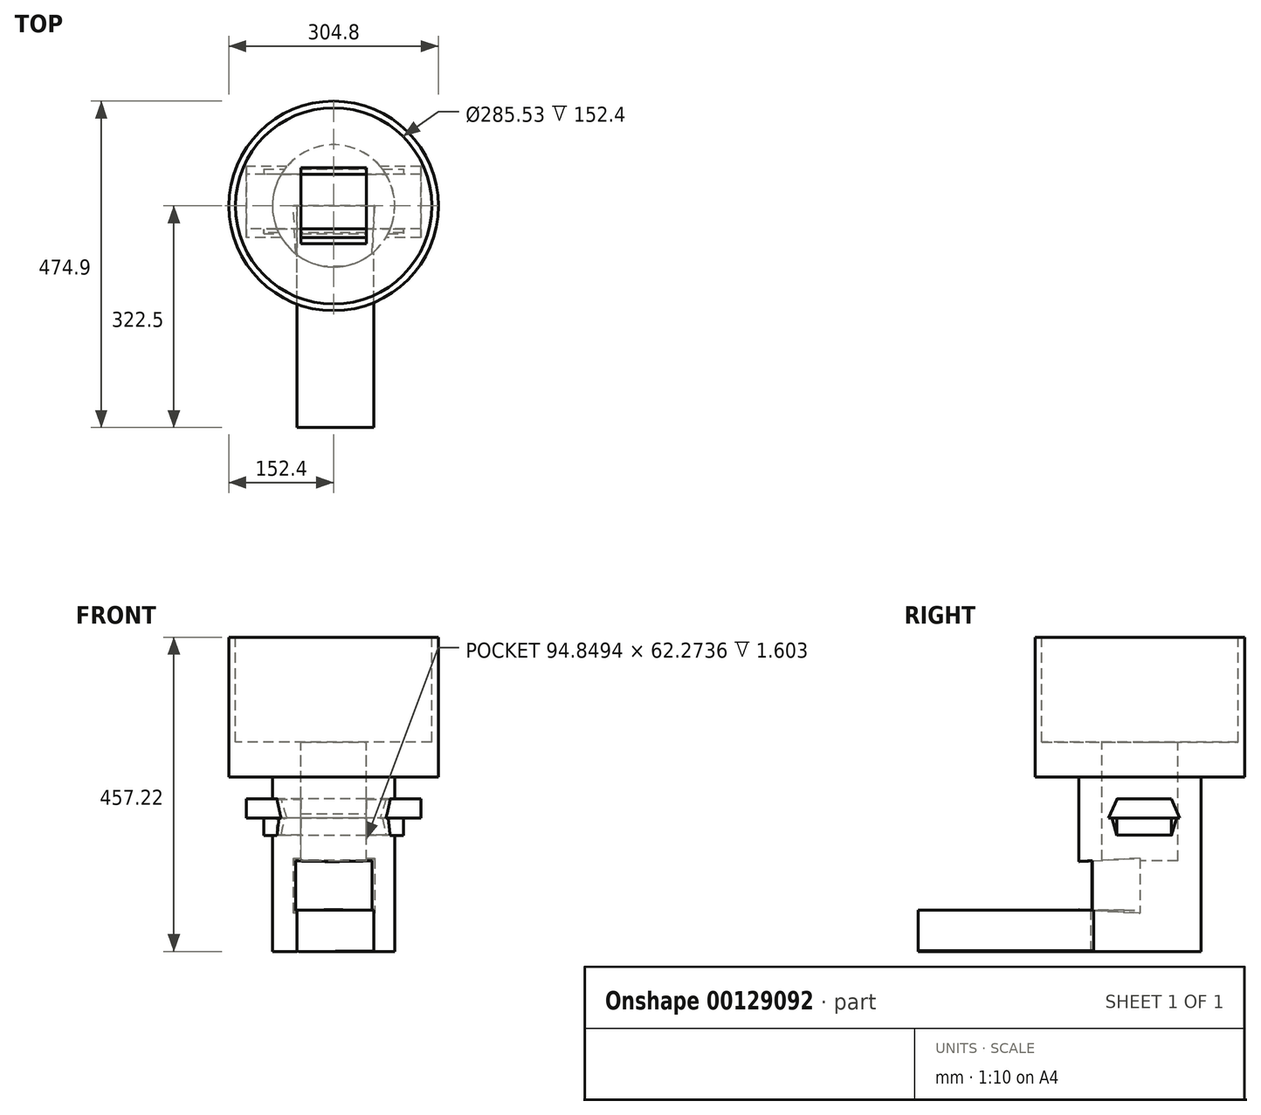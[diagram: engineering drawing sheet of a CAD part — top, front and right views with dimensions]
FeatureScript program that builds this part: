
annotation { "Feature Type Name" : "Feature", "Feature Type Description" : "" }
export const myFeature = defineFeature(function(context is Context, id is Id, definition is map)
    precondition{}
    {
        {
            var Q0;
            Q0=qCreatedBy(makeId("Top.planeOp"),FACE);
            var sketch = newSketch(context, id + "F0", { "sketchPlane" : qUnion([Q0])});
            skCircle(sketch, "E0", {"center": v(0, 0) * mm, "radius": 152.4 * mm});
            skSolve(sketch);
        }
        {
            var Q0;
            Q0 = qSketchRegion(id + "F0", true);
            extrude(context, id + "F1", {"entities" : qUnion([Q0]), "depth" : 203.2 * mm});
        }
        {
            var Q0;
            Q0=makeQuery(id+"F1.opExtrude","CAP_FACE",FACE,{"disambiguationData":[OSD([sQuery(id+"F0.wireOp",EDGE,"E0")])],"isStart":true});
            var sketch = newSketch(context, id + "F2", { "sketchPlane" : qUnion([Q0])});
            skCircle(sketch, "E1", {"center": v(0, 0) * mm, "radius": 88.9 * mm});
            skSolve(sketch);
        }
        {
            var Q0;
            Q0=makeQuery(id+"F2.imprint","IMPRINT",FACE,{"disambiguationData":[TD([[makeQuery(id+"F2.imprint","IMPRINT",EDGE,{"derivedFrom":sQuery(id+"F2.wireOp",EDGE,"E1")}),1.0]])]});
            extrude(context, id + "F3", {"entities" : qUnion([Q0]), "operationType" : NewBodyOperationType.ADD, "depth" : 254 * mm});
        }
        {
            var Q0;
            Q0=qCreatedBy(makeId("Front.planeOp"),FACE);
            var sketch = newSketch(context, id + "F4", { "sketchPlane" : qUnion([Q0])});
            skLineSegment(sketch, "E2.bottom", {"start": v(-58.57, -118.54) * mm, "end": v(59.53, -118.54) * mm});
            skLineSegment(sketch, "E2.top", {"start": v(-58.57, -198.23) * mm, "end": v(59.53, -198.23) * mm});
            skLineSegment(sketch, "E2.left", {"start": v(-58.57, -118.54) * mm, "end": v(-58.57, -198.23) * mm});
            skLineSegment(sketch, "E2.right", {"start": v(59.53, -118.54) * mm, "end": v(59.53, -198.23) * mm});
            skSolve(sketch);
        }
        {
            var Q0;
            Q0 = qSketchRegion(id + "F4", true);
            var Q1;
            Q1=makeQuery(id+"F1.opExtrude","SWEPT_BODY",BODY,{"disambiguationData":[OSD([sQuery(id+"F0.wireOp",EDGE,"E0")])]});
            extrude(context, id + "F5", {"entities" : qUnion([Q0]), "operationType" : NewBodyOperationType.REMOVE, "endBoundEntityBody" : qUnion([Q1]), "depth" : 152.4 * mm, "hasDraft" : true, "draftAngle" : 3 * degree, "draftPullDirection" : true});
        }
        {
            var Q0;
            Q0=makeQuery(id+"F1.opExtrude","CAP_FACE",FACE,{"disambiguationData":[OSD([sQuery(id+"F0.wireOp",EDGE,"E0")])],"isStart":false});
            var sketch = newSketch(context, id + "F6", { "sketchPlane" : qUnion([Q0])});
            skLineSegment(sketch, "E3.bottom", {"start": v(47.42, 55.23) * mm, "end": v(-47.42, 55.23) * mm});
            skLineSegment(sketch, "E3.top", {"start": v(47.42, -55.23) * mm, "end": v(-47.42, -55.23) * mm});
            skLineSegment(sketch, "E3.left", {"start": v(47.42, 55.23) * mm, "end": v(47.42, -55.23) * mm});
            skLineSegment(sketch, "E3.right", {"start": v(-47.42, 55.23) * mm, "end": v(-47.42, -55.23) * mm});
            skPoint(sketch, "E3.middle", {"position": v(0, 0) * mm});
            skSolve(sketch);
        }
        {
            var Q0;
            Q0=makeQuery(id+"F6.imprint","IMPRINT",FACE,{"disambiguationData":[TD([[makeQuery(id+"F6.imprint","IMPRINT",EDGE,{"derivedFrom":sQuery(id+"F6.wireOp",EDGE,"E3.bottom")}),1.0]])]});
            var Q1;
            Q1=sQuery(id+"F6.wireOp",EDGE,"bKwGgYF3-I8BH-BRHj-HJDU-NQ5mYMks3KpP");
            extrude(context, id + "F7", {"entities" : qUnion([Q0]), "operationType" : NewBodyOperationType.REMOVE, "surfaceEntities" : qUnion([Q1]), "oppositeDirection" : true, "depth" : 325.12 * mm});
        }
        {
            var Q0;
            Q0=makeQuery(id+"F1.opExtrude","CAP_FACE",FACE,{"disambiguationData":[OSD([sQuery(id+"F0.wireOp",EDGE,"E0")])],"isStart":false});
            var sketch = newSketch(context, id + "F8", { "sketchPlane" : qUnion([Q0])});
            skCircle(sketch, "E4", {"center": v(0, 0) * mm, "radius": 142.76 * mm});
            skSolve(sketch);
        }
        {
            var Q0;
            Q0 = qSketchRegion(id + "F8", true);
            extrude(context, id + "F9", {"entities" : qUnion([Q0]), "operationType" : NewBodyOperationType.REMOVE, "oppositeDirection" : true, "depth" : 152.4 * mm});
        }
        {
            var Q0;
            Q0=qCreatedBy(makeId("Right.planeOp"),FACE);
            var sketch = newSketch(context, id + "F10", { "sketchPlane" : qUnion([Q0])});
            skLineSegment(sketch, "E5.bottom", {"start": v(-33.68, -32.13) * mm, "end": v(46.01, -32.13) * mm});
            skLineSegment(sketch, "E5.top", {"start": v(-33.68, -84.93) * mm, "end": v(46.01, -84.93) * mm});
            skLineSegment(sketch, "E5.left", {"start": v(-33.68, -32.13) * mm, "end": v(-33.68, -84.93) * mm});
            skLineSegment(sketch, "E5.right", {"start": v(46.01, -32.13) * mm, "end": v(46.01, -84.93) * mm});
            skSolve(sketch);
        }
        {
            var Q0;
            Q0 = qSketchRegion(id + "F10", true);
            extrude(context, id + "F11", {"entities" : qUnion([Q0]), "operationType" : NewBodyOperationType.REMOVE, "depth" : 101.6 * mm, "hasSecondDirection" : true, "secondDirectionOppositeDirection" : true, "secondDirectionDepth" : 101.6 * mm});
        }
        {
            var Q0;
            Q0=qCreatedBy(makeId("Right.planeOp"),FACE);
            var sketch = newSketch(context, id + "F12", { "sketchPlane" : qUnion([Q0])});
            skLineSegment(sketch, "E6", {"start": v(-33.24, -31.91) * mm, "end": v(45.95, -31.91) * mm});
            skPoint(sketch, "E7", {"position": v(45.72, -73) * mm});
            skLineSegment(sketch, "E8", {"start": v(45.95, -31.91) * mm, "end": v(57.69, -59.65) * mm});
            skLineSegment(sketch, "E9", {"start": v(57.69, -59.65) * mm, "end": v(-45.8, -59.65) * mm});
            skLineSegment(sketch, "E10", {"start": v(-45.8, -59.65) * mm, "end": v(-33.24, -31.91) * mm});
            skLineSegment(sketch, "E11", {"start": v(45.95, -31.91) * mm, "end": v(-33.24, -31.91) * mm});
            skSolve(sketch);
        }
        {
            var Q0;
            Q0 = qSketchRegion(id + "F12", true);
            extrude(context, id + "F13", {"entities" : qUnion([Q0]), "operationType" : NewBodyOperationType.ADD, "depth" : 127 * mm, "hasSecondDirection" : true, "secondDirectionOppositeDirection" : true, "secondDirectionDepth" : 127 * mm});
        }
        {
            var Q0;
            Q0=qCreatedBy(makeId("Right.planeOp"),FACE);
            var sketch = newSketch(context, id + "F14", { "sketchPlane" : qUnion([Q0])});
            skLineSegment(sketch, "E12", {"start": v(-40.28, -59.6) * mm, "end": v(-33.77, -85.4) * mm});
            skLineSegment(sketch, "E13", {"start": v(-33.77, -85.4) * mm, "end": v(-33.77, -59.79) * mm});
            skLineSegment(sketch, "E14", {"start": v(-33.77, -59.79) * mm, "end": v(-40.28, -59.6) * mm});
            skLineSegment(sketch, "E15", {"start": v(45.72, -59.62) * mm, "end": v(53.64, -59.62) * mm});
            skLineSegment(sketch, "E16", {"start": v(53.64, -59.62) * mm, "end": v(45.8, -85.16) * mm});
            skLineSegment(sketch, "E17", {"start": v(45.8, -85.16) * mm, "end": v(45.72, -59.62) * mm});
            skSolve(sketch);
        }
        {
            var Q0;
            Q0 = qSketchRegion(id + "F14", true);
            extrude(context, id + "F15", {"entities" : qUnion([Q0]), "operationType" : NewBodyOperationType.ADD, "depth" : 101.6 * mm, "hasSecondDirection" : true, "secondDirectionOppositeDirection" : true, "secondDirectionDepth" : 101.6 * mm});
        }
        {
            var Q0;
            Q0=qCreatedBy(makeId("Front.planeOp"),FACE);
            var sketch = newSketch(context, id + "F16", { "sketchPlane" : qUnion([Q0])});
            skLineSegment(sketch, "E18", {"start": v(-52.97, -193.63) * mm, "end": v(58.33, -193.63) * mm});
            skLineSegment(sketch, "E19", {"start": v(58.33, -193.63) * mm, "end": v(58.33, -252.94) * mm});
            skLineSegment(sketch, "E20", {"start": v(-52.97, -193.63) * mm, "end": v(-52.97, -254.02) * mm});
            skLineSegment(sketch, "E21", {"start": v(-52.97, -254.02) * mm, "end": v(58.33, -252.94) * mm});
            skSolve(sketch);
        }
        {
            var Q0;
            Q0 = qSketchRegion(id + "F16", true);
            extrude(context, id + "F17", {"entities" : qUnion([Q0]), "operationType" : NewBodyOperationType.ADD, "depth" : 322.5 * mm});
        }
    });
